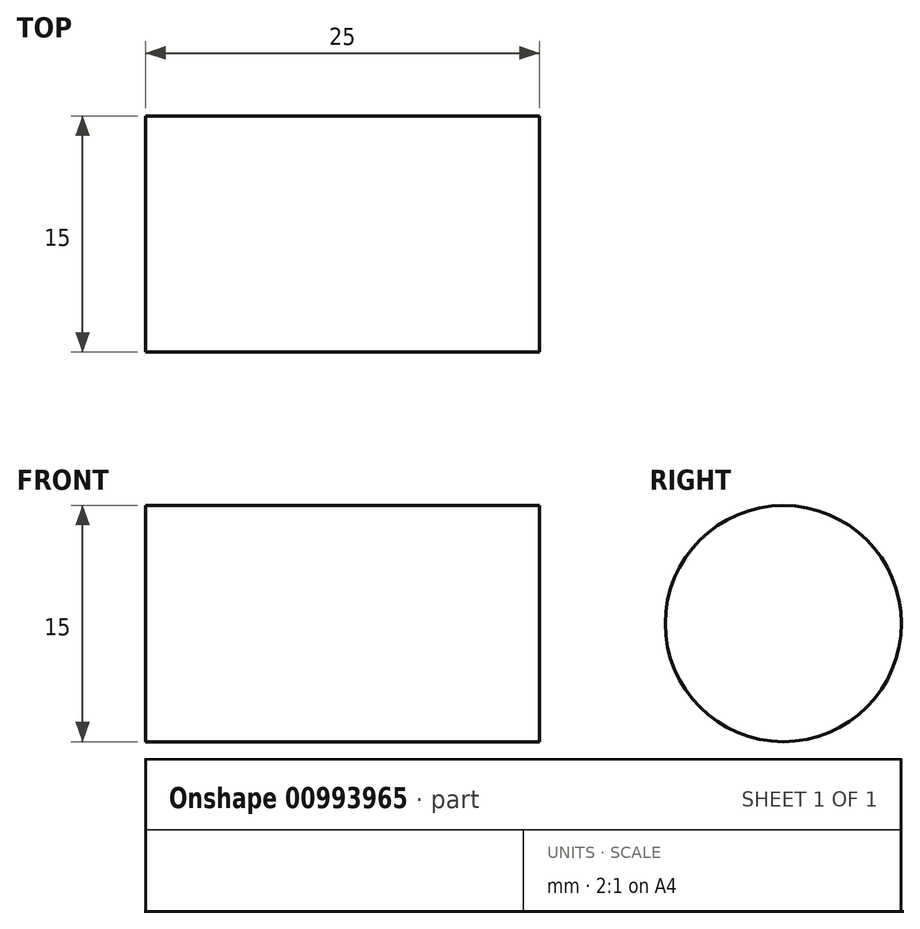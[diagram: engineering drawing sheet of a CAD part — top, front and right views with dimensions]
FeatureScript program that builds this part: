
annotation { "Feature Type Name" : "Feature", "Feature Type Description" : "" }
export const myFeature = defineFeature(function(context is Context, id is Id, definition is map)
    precondition{}
    {
        {
            var Q0;
            Q0=qCreatedBy(makeId("Right.planeOp"),FACE);
            var sketch = newSketch(context, id + "F0", { "sketchPlane" : qUnion([Q0])});
            skCircle(sketch, "E0", {"center": v(0, 0) * mm, "radius": 7.5 * mm});
            skSolve(sketch);
        }
        {
            var Q0;
            Q0 = qSketchRegion(id + "F0", true);
            extrude(context, id + "F1", {"entities" : qUnion([Q0]), "depth" : 25 * mm, "offsetDistance" : 25 * mm});
        }
    });
